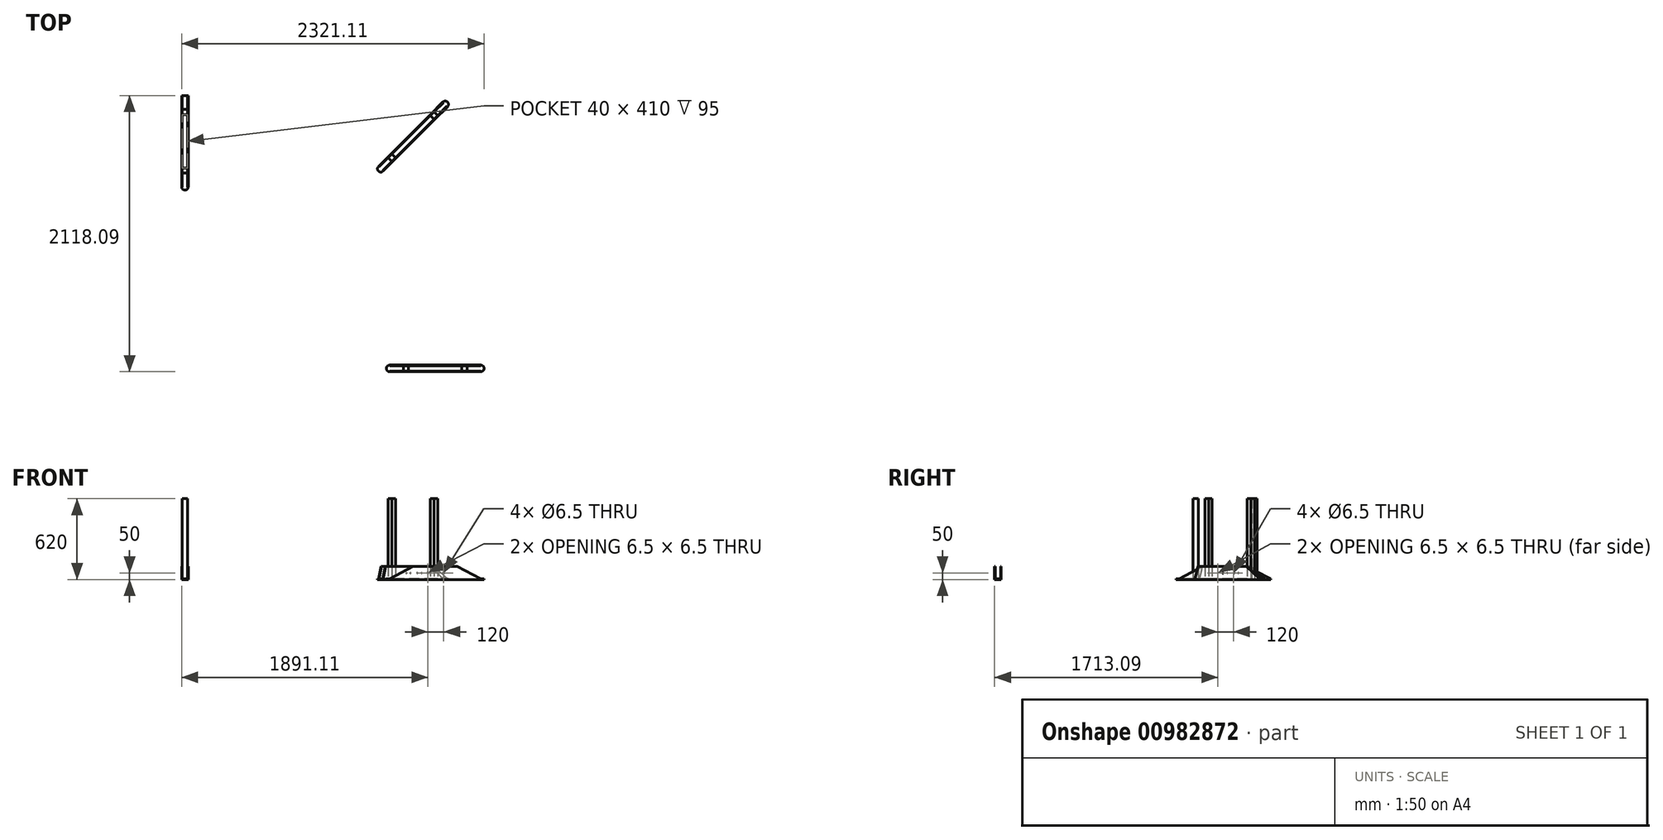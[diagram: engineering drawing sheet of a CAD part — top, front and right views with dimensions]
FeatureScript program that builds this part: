
annotation { "Feature Type Name" : "Feature", "Feature Type Description" : "" }
export const myFeature = defineFeature(function(context is Context, id is Id, definition is map)
    precondition{}
    {
        {
            var Q0;
            Q0=qCreatedBy(makeId("Top.planeOp"),FACE);
            var sketch = newSketch(context, id + "F0", { "sketchPlane" : qUnion([Q0])});
            skLineSegment(sketch, "E0", {"start": v(-1484.96, 152.2) * mm, "end": v(-1484.96, 852.2) * mm});
            skLineSegment(sketch, "E1", {"start": v(-1434.96, 852.2) * mm, "end": v(-1434.96, 152.2) * mm});
            skLineSegment(sketch, "E2.left", {"start": v(-1479.96, 502.2) * mm, "end": v(-1479.96, 542.2) * mm});
            skLineSegment(sketch, "E2.right", {"start": v(-1439.96, 502.2) * mm, "end": v(-1439.96, 542.2) * mm});
            skLineSegment(sketch, "E3.left", {"start": v(-1479.96, 202.2) * mm, "end": v(-1479.96, 242.2) * mm});
            skLineSegment(sketch, "E3.right", {"start": v(-1439.96, 202.2) * mm, "end": v(-1439.96, 242.2) * mm});
            skLineSegment(sketch, "E4", {"start": v(111.15, -1215.89) * mm, "end": v(811.15, -1215.89) * mm});
            skLineSegment(sketch, "E5", {"start": v(811.15, -1265.89) * mm, "end": v(111.15, -1265.89) * mm});
            skLineSegment(sketch, "E6.bottom", {"start": v(331.15, -1260.89) * mm, "end": v(421.15, -1260.89) * mm});
            skLineSegment(sketch, "E6.top", {"start": v(331.15, -1220.89) * mm, "end": v(421.15, -1220.89) * mm});
            skLineSegment(sketch, "E7.bottom", {"start": v(511.15, -1260.89) * mm, "end": v(591.15, -1260.89) * mm});
            skLineSegment(sketch, "E7.top", {"start": v(511.15, -1220.89) * mm, "end": v(591.15, -1220.89) * mm});
            skLineSegment(sketch, "E8", {"start": v(43.16, 326.14) * mm, "end": v(392.98, 675.97) * mm});
            skLineSegment(sketch, "E9", {"start": v(78.51, 290.79) * mm, "end": v(428.33, 640.61) * mm});
            skLineSegment(sketch, "E10", {"start": v(428.33, 640.61) * mm, "end": v(449.74, 662.02) * mm});
            skLineSegment(sketch, "E11", {"start": v(392.98, 675.97) * mm, "end": v(414.39, 697.38) * mm});
            skLineSegment(sketch, "E12", {"start": v(414.39, 697.38) * mm, "end": v(446.01, 729) * mm});
            skLineSegment(sketch, "E13", {"start": v(485.1, 697.38) * mm, "end": v(449.74, 662.02) * mm});
            skLineSegment(sketch, "E14", {"start": v(485.1, 697.38) * mm, "end": v(555.8, 768.09) * mm});
            skLineSegment(sketch, "E15", {"start": v(555.8, 768.09) * mm, "end": v(520.45, 803.44) * mm});
            skLineSegment(sketch, "E16", {"start": v(520.45, 803.44) * mm, "end": v(446.01, 729) * mm});
            skLineSegment(sketch, "E17", {"start": v(78.51, 290.79) * mm, "end": v(60.83, 273.11) * mm});
            skLineSegment(sketch, "E18", {"start": v(43.16, 326.14) * mm, "end": v(25.48, 308.47) * mm});
            skLineSegment(sketch, "E19", {"start": v(241.15, 517.06) * mm, "end": v(269.43, 545.35) * mm});
            skLineSegment(sketch, "E20", {"start": v(297.71, 517.06) * mm, "end": v(269.43, 488.78) * mm});
            skLineSegment(sketch, "E21", {"start": v(280.23, 556.15) * mm, "end": v(308.52, 584.43) * mm});
            skLineSegment(sketch, "E22", {"start": v(333.07, 552.42) * mm, "end": v(304.79, 524.13) * mm});
            skLineSegment(sketch, "E23", {"start": v(-1484.96, 852.2) * mm, "end": v(-1434.96, 852.2) * mm});
            skLineSegment(sketch, "E24", {"start": v(-1484.96, 152.2) * mm, "end": v(-1434.96, 152.2) * mm});
            skLineSegment(sketch, "E25", {"start": v(811.15, -1215.89) * mm, "end": v(811.15, -1265.89) * mm});
            skLineSegment(sketch, "E26", {"start": v(111.15, -1215.89) * mm, "end": v(111.15, -1265.89) * mm});
            skLineSegment(sketch, "E27", {"start": v(25.48, 308.47) * mm, "end": v(60.83, 273.11) * mm});
            skLineSegment(sketch, "E28", {"start": v(241.15, 517.06) * mm, "end": v(29.01, 304.93) * mm});
            skLineSegment(sketch, "E29", {"start": v(269.43, 488.78) * mm, "end": v(57.3, 276.65) * mm});
            skLineSegment(sketch, "E30", {"start": v(297.71, 517.06) * mm, "end": v(552.27, 771.62) * mm});
            skLineSegment(sketch, "E31", {"start": v(269.43, 545.35) * mm, "end": v(523.99, 799.9) * mm});
            skLineSegment(sketch, "E32", {"start": v(511.15, -1260.89) * mm, "end": v(811.15, -1260.89) * mm});
            skLineSegment(sketch, "E33", {"start": v(511.15, -1220.89) * mm, "end": v(811.15, -1220.89) * mm});
            skLineSegment(sketch, "E34", {"start": v(591.15, -1220.89) * mm, "end": v(111.15, -1220.89) * mm});
            skLineSegment(sketch, "E35", {"start": v(591.15, -1260.89) * mm, "end": v(111.15, -1260.89) * mm});
            skLineSegment(sketch, "E36", {"start": v(-1439.96, 202.2) * mm, "end": v(-1439.96, 152.2) * mm});
            skLineSegment(sketch, "E37", {"start": v(-1479.96, 202.2) * mm, "end": v(-1479.96, 152.2) * mm});
            skLineSegment(sketch, "E38", {"start": v(-1479.96, 242.2) * mm, "end": v(-1479.96, 852.2) * mm});
            skLineSegment(sketch, "E39", {"start": v(-1439.96, 242.2) * mm, "end": v(-1439.96, 852.2) * mm});
            skArc(sketch, "E40", {"start": v(-1484.96, 152.2) * mm, "mid": v(-1459.96, 127.2) * mm, "end": v(-1434.96, 152.2) * mm});
            skArc(sketch, "E41", {"start": v(-1484.96, 852.2) * mm, "mid": v(-1459.96, 877.2) * mm, "end": v(-1434.96, 852.2) * mm});
            skArc(sketch, "E42", {"start": v(25.48, 308.47) * mm, "mid": v(25.48, 273.11) * mm, "end": v(60.83, 273.11) * mm});
            skArc(sketch, "E43", {"start": v(555.8, 768.09) * mm, "mid": v(555.8, 803.44) * mm, "end": v(520.45, 803.44) * mm});
            skArc(sketch, "E44", {"start": v(811.15, -1265.89) * mm, "mid": v(836.15, -1240.89) * mm, "end": v(811.15, -1215.89) * mm});
            skArc(sketch, "E45", {"start": v(111.15, -1215.89) * mm, "mid": v(86.15, -1240.89) * mm, "end": v(111.15, -1265.89) * mm});
            skLineSegment(sketch, "E46.bottom", {"start": v(-1479.96, 747.2) * mm, "end": v(-1439.96, 747.2) * mm});
            skLineSegment(sketch, "E46.top", {"start": v(-1479.96, 707.2) * mm, "end": v(-1439.96, 707.2) * mm});
            skLineSegment(sketch, "E46.left", {"start": v(-1479.96, 747.2) * mm, "end": v(-1479.96, 707.2) * mm});
            skLineSegment(sketch, "E46.right", {"start": v(-1439.96, 747.2) * mm, "end": v(-1439.96, 707.2) * mm});
            skLineSegment(sketch, "E47.bottom", {"start": v(-1439.96, 257.2) * mm, "end": v(-1479.96, 257.2) * mm});
            skLineSegment(sketch, "E47.top", {"start": v(-1439.96, 297.2) * mm, "end": v(-1479.96, 297.2) * mm});
            skLineSegment(sketch, "E47.left", {"start": v(-1439.96, 257.2) * mm, "end": v(-1439.96, 297.2) * mm});
            skLineSegment(sketch, "E47.right", {"start": v(-1479.96, 257.2) * mm, "end": v(-1479.96, 297.2) * mm});
            skLineSegment(sketch, "E48.bottom", {"start": v(216.15, -1260.89) * mm, "end": v(256.15, -1260.89) * mm});
            skLineSegment(sketch, "E48.top", {"start": v(216.15, -1220.89) * mm, "end": v(256.15, -1220.89) * mm});
            skLineSegment(sketch, "E48.left", {"start": v(216.15, -1260.89) * mm, "end": v(216.15, -1220.89) * mm});
            skLineSegment(sketch, "E48.right", {"start": v(256.15, -1260.89) * mm, "end": v(256.15, -1220.89) * mm});
            skLineSegment(sketch, "E49.bottom", {"start": v(666.15, -1260.89) * mm, "end": v(706.15, -1260.89) * mm});
            skLineSegment(sketch, "E49.top", {"start": v(666.15, -1220.89) * mm, "end": v(706.15, -1220.89) * mm});
            skLineSegment(sketch, "E49.left", {"start": v(666.15, -1260.89) * mm, "end": v(666.15, -1220.89) * mm});
            skLineSegment(sketch, "E49.right", {"start": v(706.15, -1260.89) * mm, "end": v(706.15, -1220.89) * mm});
            skLineSegment(sketch, "E50", {"start": v(128, 347.36) * mm, "end": v(99.72, 375.64) * mm});
            skLineSegment(sketch, "E51", {"start": v(156.3, 375.64) * mm, "end": v(128, 403.93) * mm});
            skLineSegment(sketch, "E52", {"start": v(481.56, 700.91) * mm, "end": v(453.28, 729.2) * mm});
            skLineSegment(sketch, "E53", {"start": v(453.28, 672.63) * mm, "end": v(425, 700.91) * mm});
            skSolve(sketch);
        }
        {
            var Q0;
            {var subQ0=sQuery(id+"F0.wireOp",EDGE,"E6.left");Q0=makeQuery(id+"F0.imprint","IMPRINT",FACE,{"disambiguationData":[TD([[makeQuery(id+"F0.imprint","IMPRINT",EDGE,{"derivedFrom":subQ0}),1.0]])]});}
            var Q1;
            {var subQ0=sQuery(id+"F0.wireOp",EDGE,"E6.right");Q1=makeQuery(id+"F0.imprint","IMPRINT",FACE,{"disambiguationData":[TD([[makeQuery(id+"F0.imprint","IMPRINT",EDGE,{"derivedFrom":subQ0}),-1.0]])]});}
            var Q2;
            Q2=makeQuery(id+"F0.imprint","IMPRINT",FACE,{"disambiguationData":[TD([[makeQuery(id+"F0.imprint","IMPRINT",EDGE,{"derivedFrom":sQuery(id+"F0.wireOp",EDGE,"E7.right")}),-1.0]])]});
            var Q3;
            {var subQ0=sQuery(id+"F0.wireOp",EDGE,"E44");Q3=makeQuery(id+"F0.imprint","IMPRINT",FACE,{"disambiguationData":[TD([[makeQuery(id+"F0.imprint","IMPRINT",EDGE,{"derivedFrom":subQ0}),1.0]])]});}
            var Q4;
            {var subQ0=sQuery(id+"F0.wireOp",EDGE,"E45");Q4=makeQuery(id+"F0.imprint","IMPRINT",FACE,{"disambiguationData":[TD([[makeQuery(id+"F0.imprint","IMPRINT",EDGE,{"derivedFrom":subQ0}),1.0]])]});}
            var Q5;
            {var subQ0=sQuery(id+"F0.wireOp",EDGE,"E42");Q5=makeQuery(id+"F0.imprint","IMPRINT",FACE,{"disambiguationData":[TD([[makeQuery(id+"F0.imprint","IMPRINT",EDGE,{"derivedFrom":subQ0}),1.0]])]});}
            var Q6;
            Q6=makeQuery(id+"F0.imprint","IMPRINT",FACE,{"disambiguationData":[TD([[makeQuery(id+"F0.imprint","IMPRINT",EDGE,{"derivedFrom":sQuery(id+"F0.wireOp",EDGE,"d1bdfd27-d275-4df7-8525-5a3e29133dde")}),1.0]])]});
            var Q7;
            {var subQ0=sQuery(id+"F0.wireOp",EDGE,"a0a4fd81-97b6-4ab5-b91d-3bcc11f45807");Q7=makeQuery(id+"F0.imprint","IMPRINT",FACE,{"disambiguationData":[TD([[makeQuery(id+"F0.imprint","IMPRINT",EDGE,{"derivedFrom":subQ0}),1.0]])]});}
            var Q8;
            {var subQ5=sQuery(id+"F0.wireOp",EDGE,"5f6abebd-f6dd-4679-b2fa-9a6ba4823ef2");Q8=makeQuery(id+"F0.imprint","IMPRINT",FACE,{"disambiguationData":[TD([[makeQuery(id+"F0.imprint","IMPRINT",EDGE,{"derivedFrom":subQ5}),1.0]])]});}
            var Q9;
            {var subQ0=sQuery(id+"F0.wireOp",EDGE,"E43");Q9=makeQuery(id+"F0.imprint","IMPRINT",FACE,{"disambiguationData":[TD([[makeQuery(id+"F0.imprint","IMPRINT",EDGE,{"derivedFrom":subQ0}),1.0]])]});}
            var Q10;
            {var subQ0=sQuery(id+"F0.wireOp",EDGE,"E40");Q10=makeQuery(id+"F0.imprint","IMPRINT",FACE,{"disambiguationData":[TD([[makeQuery(id+"F0.imprint","IMPRINT",EDGE,{"derivedFrom":subQ0}),1.0]])]});}
            var Q11;
            Q11=makeQuery(id+"F0.imprint","IMPRINT",FACE,{"disambiguationData":[TD([[makeQuery(id+"F0.imprint","IMPRINT",EDGE,{"derivedFrom":sQuery(id+"F0.wireOp",EDGE,"E3.bottom")}),-1.0]])]});
            var Q12;
            {var subQ0=sQuery(id+"F0.wireOp",EDGE,"E2.bottom");Q12=makeQuery(id+"F0.imprint","IMPRINT",FACE,{"disambiguationData":[TD([[makeQuery(id+"F0.imprint","IMPRINT",EDGE,{"derivedFrom":subQ0}),-1.0]])]});}
            var Q13;
            {var subQ0=sQuery(id+"F0.wireOp",EDGE,"E41");Q13=makeQuery(id+"F0.imprint","IMPRINT",FACE,{"disambiguationData":[TD([[makeQuery(id+"F0.imprint","IMPRINT",EDGE,{"derivedFrom":subQ0}),-1.0]])]});}
            var Q14;
            {var subQ0=sQuery(id+"F0.wireOp",EDGE,"E2.top");Q14=makeQuery(id+"F0.imprint","IMPRINT",FACE,{"disambiguationData":[TD([[makeQuery(id+"F0.imprint","IMPRINT",EDGE,{"derivedFrom":subQ0}),1.0]])]});}
            var Q15;
            {var subQ3=sQuery(id+"F0.wireOp",EDGE,"E3.left");Q15=makeQuery(id+"F0.imprint","IMPRINT",FACE,{"disambiguationData":[TD([[makeQuery(id+"F0.imprint","IMPRINT",EDGE,{"derivedFrom":subQ3}),-1.0]])]});}
            var Q16;
            {var subQ5=sQuery(id+"F0.wireOp",EDGE,"xkCS3JtT-tGRa-9SgF-1onI-mmZA8H57qGDA");Q16=makeQuery(id+"F0.imprint","IMPRINT",FACE,{"disambiguationData":[TD([[makeQuery(id+"F0.imprint","IMPRINT",EDGE,{"derivedFrom":subQ5}),1.0]])]});}
            var Q17;
            {var subQ5=sQuery(id+"F0.wireOp",EDGE,"E48.left");Q17=makeQuery(id+"F0.imprint","IMPRINT",FACE,{"disambiguationData":[TD([[makeQuery(id+"F0.imprint","IMPRINT",EDGE,{"derivedFrom":subQ5}),1.0]])]});}
            var Q18;
            {var subQ0=sQuery(id+"F0.wireOp",EDGE,"E48.right");Q18=makeQuery(id+"F0.imprint","IMPRINT",FACE,{"disambiguationData":[TD([[makeQuery(id+"F0.imprint","IMPRINT",EDGE,{"derivedFrom":subQ0}),-1.0]])]});}
            var Q19;
            {var subQ5=sQuery(id+"F0.wireOp",EDGE,"E49.right");Q19=makeQuery(id+"F0.imprint","IMPRINT",FACE,{"disambiguationData":[TD([[makeQuery(id+"F0.imprint","IMPRINT",EDGE,{"derivedFrom":subQ5}),-1.0]])]});}
            var Q20;
            {var subQ5=sQuery(id+"F0.wireOp",EDGE,"E50");Q20=makeQuery(id+"F0.imprint","IMPRINT",FACE,{"disambiguationData":[TD([[makeQuery(id+"F0.imprint","IMPRINT",EDGE,{"derivedFrom":subQ5}),1.0]])]});}
            var Q21;
            {var subQ5=sQuery(id+"F0.wireOp",EDGE,"E52");Q21=makeQuery(id+"F0.imprint","IMPRINT",FACE,{"disambiguationData":[TD([[makeQuery(id+"F0.imprint","IMPRINT",EDGE,{"derivedFrom":subQ5}),-1.0]])]});}
            var Q22;
            {var subQ0=sQuery(id+"F0.wireOp",EDGE,"E46.top");Q22=makeQuery(id+"F0.imprint","IMPRINT",FACE,{"disambiguationData":[TD([[makeQuery(id+"F0.imprint","IMPRINT",EDGE,{"derivedFrom":subQ0}),-1.0]])]});}
            var Q23;
            {var subQ5=sQuery(id+"F0.wireOp",EDGE,"E46.bottom");Q23=makeQuery(id+"F0.imprint","IMPRINT",FACE,{"disambiguationData":[TD([[makeQuery(id+"F0.imprint","IMPRINT",EDGE,{"derivedFrom":subQ5}),1.0]])]});}
            var Q24;
            {var subQ8=sQuery(id+"F0.wireOp",EDGE,"E19");Q24=makeQuery(id+"F0.imprint","IMPRINT",FACE,{"disambiguationData":[TD([[makeQuery(id+"F0.imprint","IMPRINT",EDGE,{"derivedFrom":subQ8}),-1.0]])]});}
            extrude(context, id + "F1", {"entities" : qUnion([Q0, Q1, Q2, Q3, Q4, Q5, Q6, Q7, Q8, Q9, Q10, Q11, Q12, Q13, Q14, Q15, Q16, Q17, Q18, Q19, Q20, Q21, Q22, Q23, Q24]), "depth" : 5 * mm, "offsetDistance" : 25 * mm});
        }
        {
            var Q0;
            {var subQ0=sQuery(id+"F0.wireOp",EDGE,"E50");Q0=makeQuery(id+"F0.imprint","IMPRINT",FACE,{"disambiguationData":[TD([[makeQuery(id+"F0.imprint","IMPRINT",EDGE,{"derivedFrom":subQ0}),-1.0]])]});}
            var Q1;
            {var subQ0=sQuery(id+"F0.wireOp",EDGE,"E52");Q1=makeQuery(id+"F0.imprint","IMPRINT",FACE,{"disambiguationData":[TD([[makeQuery(id+"F0.imprint","IMPRINT",EDGE,{"derivedFrom":subQ0}),1.0]])]});}
            var Q2;
            Q2=makeQuery(id+"F0.imprint","IMPRINT",FACE,{"disambiguationData":[TD([[makeQuery(id+"F0.imprint","IMPRINT",EDGE,{"derivedFrom":sQuery(id+"F0.wireOp",EDGE,"E49.bottom")}),1.0]])]});
            var Q3;
            Q3=makeQuery(id+"F0.imprint","IMPRINT",FACE,{"disambiguationData":[TD([[makeQuery(id+"F0.imprint","IMPRINT",EDGE,{"derivedFrom":sQuery(id+"F0.wireOp",EDGE,"E48.bottom")}),1.0]])]});
            var Q4;
            Q4=makeQuery(id+"F0.imprint","IMPRINT",FACE,{"disambiguationData":[TD([[makeQuery(id+"F0.imprint","IMPRINT",EDGE,{"derivedFrom":sQuery(id+"F0.wireOp",EDGE,"E46.bottom")}),-1.0]])]});
            var Q5;
            Q5=makeQuery(id+"F0.imprint","IMPRINT",FACE,{"disambiguationData":[TD([[makeQuery(id+"F0.imprint","IMPRINT",EDGE,{"derivedFrom":sQuery(id+"F0.wireOp",EDGE,"E47.bottom")}),-1.0]])]});
            extrude(context, id + "F2", {"entities" : qUnion([Q0, Q1, Q2, Q3, Q4, Q5]), "depth" : 620 * mm, "offsetDistance" : 25 * mm});
        }
        {
            var Q0;
            {var subQ1=sQuery(id+"F0.wireOp",EDGE,"E0");Q0=makeQuery(id+"F0.imprint","IMPRINT",FACE,{"disambiguationData":[TD([[makeQuery(id+"F0.imprint","IMPRINT",EDGE,{"derivedFrom":subQ1}),-1.0]])]});}
            var Q1;
            {var subQ1=sQuery(id+"F0.wireOp",EDGE,"E1");Q1=makeQuery(id+"F0.imprint","IMPRINT",FACE,{"disambiguationData":[TD([[makeQuery(id+"F0.imprint","IMPRINT",EDGE,{"derivedFrom":subQ1}),-1.0]])]});}
            var Q2;
            Q2=makeQuery(id+"F0.imprint","IMPRINT",FACE,{"disambiguationData":[TD([[makeQuery(id+"F0.imprint","IMPRINT",EDGE,{"derivedFrom":sQuery(id+"F0.wireOp",EDGE,"E8")}),-1.0]])]});
            var Q3;
            Q3=makeQuery(id+"F0.imprint","IMPRINT",FACE,{"disambiguationData":[TD([[makeQuery(id+"F0.imprint","IMPRINT",EDGE,{"derivedFrom":sQuery(id+"F0.wireOp",EDGE,"E9")}),1.0]])]});
            var Q4;
            {var subQ1=sQuery(id+"F0.wireOp",EDGE,"E4");Q4=makeQuery(id+"F0.imprint","IMPRINT",FACE,{"disambiguationData":[TD([[makeQuery(id+"F0.imprint","IMPRINT",EDGE,{"derivedFrom":subQ1}),-1.0]])]});}
            var Q5;
            {var subQ1=sQuery(id+"F0.wireOp",EDGE,"E5");Q5=makeQuery(id+"F0.imprint","IMPRINT",FACE,{"disambiguationData":[TD([[makeQuery(id+"F0.imprint","IMPRINT",EDGE,{"derivedFrom":subQ1}),-1.0]])]});}
            extrude(context, id + "F3", {"entities" : qUnion([Q0, Q1, Q2, Q3, Q4, Q5]), "depth" : 100 * mm, "offsetDistance" : 25 * mm});
        }
        {
            var Q0;
            {var subQ0=sQuery(id+"F0.wireOp",EDGE,"E26");Q0=makeQuery(id+"F3.opExtrude","CAP_EDGE",EDGE,{"disambiguationData":[OSD([subQ0]),TDD([makeQuery(id+"F0.imprint","IMPRINT",EDGE,{"disambiguationData":[TD([[makeQuery(id+"F0.imprint","INTERSECT",VERTEX,{"derivedFrom":[subQ0,sQuery(id+"F0.wireOp",EDGE,"E35")]}),-1.0]])],"derivedFrom":subQ0})])],"isStart":false});}
            var Q1;
            {var subQ0=sQuery(id+"F0.wireOp",EDGE,"E26");Q1=makeQuery(id+"F3.opExtrude","CAP_EDGE",EDGE,{"disambiguationData":[OSD([subQ0]),TDD([makeQuery(id+"F0.imprint","IMPRINT",EDGE,{"disambiguationData":[TD([[makeQuery(id+"F0.imprint","INTERSECT",VERTEX,{"derivedFrom":[subQ0,sQuery(id+"F0.wireOp",EDGE,"E34")]}),1.0]])],"derivedFrom":subQ0})])],"isStart":false});}
            var Q2;
            {var subQ0=sQuery(id+"F0.wireOp",EDGE,"E25");Q2=makeQuery(id+"F3.opExtrude","CAP_EDGE",EDGE,{"disambiguationData":[OSD([subQ0]),TDD([makeQuery(id+"F0.imprint","IMPRINT",EDGE,{"disambiguationData":[TD([[makeQuery(id+"F0.imprint","INTERSECT",VERTEX,{"derivedFrom":[subQ0,sQuery(id+"F0.wireOp",EDGE,"E32")]}),-1.0]])],"derivedFrom":subQ0})])],"isStart":false});}
            var Q3;
            {var subQ0=sQuery(id+"F0.wireOp",EDGE,"E25");Q3=makeQuery(id+"F3.opExtrude","CAP_EDGE",EDGE,{"disambiguationData":[OSD([subQ0]),TDD([makeQuery(id+"F0.imprint","IMPRINT",EDGE,{"disambiguationData":[TD([[makeQuery(id+"F0.imprint","INTERSECT",VERTEX,{"derivedFrom":[subQ0,sQuery(id+"F0.wireOp",EDGE,"E33")]}),1.0]])],"derivedFrom":subQ0})])],"isStart":false});}
            chamfer(context, id + "F4", {"entities" : qUnion([Q0, Q1, Q2, Q3]), "chamferType" : ChamferType.TWO_OFFSETS, "width1" : 180 * mm, "oppositeDirection" : false, "width2" : 95 * mm, "tangentPropagation" : true});
        }
        {
            var Q0;
            {var subQ0=sQuery(id+"F0.wireOp",EDGE,"E23");Q0=makeQuery(id+"F3.opExtrude","CAP_EDGE",EDGE,{"disambiguationData":[OSD([subQ0]),TDD([makeQuery(id+"F0.imprint","IMPRINT",EDGE,{"disambiguationData":[TD([[makeQuery(id+"F0.imprint","INTERSECT",VERTEX,{"derivedFrom":[subQ0,sQuery(id+"F0.wireOp",EDGE,"E39")]}),-1.0]])],"derivedFrom":subQ0})])],"isStart":false});}
            var Q1;
            {var subQ0=sQuery(id+"F0.wireOp",EDGE,"E23");Q1=makeQuery(id+"F3.opExtrude","CAP_EDGE",EDGE,{"disambiguationData":[OSD([subQ0]),TDD([makeQuery(id+"F0.imprint","IMPRINT",EDGE,{"disambiguationData":[TD([[makeQuery(id+"F0.imprint","INTERSECT",VERTEX,{"derivedFrom":[subQ0,sQuery(id+"F0.wireOp",EDGE,"E38")]}),1.0]])],"derivedFrom":subQ0})])],"isStart":false});}
            var Q2;
            {var subQ0=sQuery(id+"F0.wireOp",EDGE,"E24");Q2=makeQuery(id+"F3.opExtrude","CAP_EDGE",EDGE,{"disambiguationData":[OSD([subQ0]),TDD([makeQuery(id+"F0.imprint","IMPRINT",EDGE,{"disambiguationData":[TD([[makeQuery(id+"F0.imprint","INTERSECT",VERTEX,{"derivedFrom":[subQ0,sQuery(id+"F0.wireOp",EDGE,"E37")]}),1.0]])],"derivedFrom":subQ0})])],"isStart":false});}
            var Q3;
            {var subQ0=sQuery(id+"F0.wireOp",EDGE,"E24");Q3=makeQuery(id+"F3.opExtrude","CAP_EDGE",EDGE,{"disambiguationData":[OSD([subQ0]),TDD([makeQuery(id+"F0.imprint","IMPRINT",EDGE,{"disambiguationData":[TD([[makeQuery(id+"F0.imprint","INTERSECT",VERTEX,{"derivedFrom":[subQ0,sQuery(id+"F0.wireOp",EDGE,"E36")]}),-1.0]])],"derivedFrom":subQ0})])],"isStart":false});}
            chamfer(context, id + "F5", {"entities" : qUnion([Q0, Q1, Q2, Q3]), "chamferType" : ChamferType.TWO_OFFSETS, "width1" : 95 * mm, "oppositeDirection" : false, "width2" : 180 * mm, "tangentPropagation" : true});
        }
        {
            var Q0;
            {var subQ0=sQuery(id+"F0.wireOp",EDGE,"E15");Q0=makeQuery(id+"F3.opExtrude","CAP_EDGE",EDGE,{"disambiguationData":[OSD([subQ0]),TDD([makeQuery(id+"F0.imprint","IMPRINT",EDGE,{"disambiguationData":[TD([[makeQuery(id+"F0.imprint","INTERSECT",VERTEX,{"derivedFrom":[subQ0,sQuery(id+"F0.wireOp",EDGE,"E30")]}),1.0]])],"derivedFrom":subQ0})])],"isStart":false});}
            var Q1;
            {var subQ0=sQuery(id+"F0.wireOp",EDGE,"E15");Q1=makeQuery(id+"F3.opExtrude","CAP_EDGE",EDGE,{"disambiguationData":[OSD([subQ0]),TDD([makeQuery(id+"F0.imprint","IMPRINT",EDGE,{"disambiguationData":[TD([[makeQuery(id+"F0.imprint","INTERSECT",VERTEX,{"derivedFrom":[subQ0,sQuery(id+"F0.wireOp",EDGE,"E31")]}),-1.0]])],"derivedFrom":subQ0})])],"isStart":false});}
            chamfer(context, id + "F6", {"entities" : qUnion([Q0, Q1]), "chamferType" : ChamferType.TWO_OFFSETS, "width1" : 142 * mm, "oppositeDirection" : false, "width2" : 95 * mm, "tangentPropagation" : true});
        }
        {
            var Q0;
            {var subQ0=sQuery(id+"F0.wireOp",EDGE,"E27");Q0=makeQuery(id+"F3.opExtrude","CAP_EDGE",EDGE,{"disambiguationData":[OSD([subQ0]),TDD([makeQuery(id+"F0.imprint","IMPRINT",EDGE,{"disambiguationData":[TD([[makeQuery(id+"F0.imprint","INTERSECT",VERTEX,{"derivedFrom":[subQ0,sQuery(id+"F0.wireOp",EDGE,"E29")]}),-1.0]])],"derivedFrom":subQ0})])],"isStart":false});}
            var Q1;
            {var subQ0=sQuery(id+"F0.wireOp",EDGE,"E27");Q1=makeQuery(id+"F3.opExtrude","CAP_EDGE",EDGE,{"disambiguationData":[OSD([subQ0]),TDD([makeQuery(id+"F0.imprint","IMPRINT",EDGE,{"disambiguationData":[TD([[makeQuery(id+"F0.imprint","INTERSECT",VERTEX,{"derivedFrom":[subQ0,sQuery(id+"F0.wireOp",EDGE,"E28")]}),1.0]])],"derivedFrom":subQ0})])],"isStart":false});}
            chamfer(context, id + "F7", {"entities" : qUnion([Q0, Q1]), "chamferType" : ChamferType.TWO_OFFSETS, "width1" : 30 * mm, "oppositeDirection" : false, "width2" : 95 * mm, "tangentPropagation" : true});
        }
        {
            var Q0;
            Q0=makeQuery(id+"F3.opExtrude","SWEPT_BODY",BODY,{"disambiguationData":[OSD([sQuery(id+"F0.wireOp",EDGE,"E1"),sQuery(id+"F0.wireOp",EDGE,"E3.right"),sQuery(id+"F0.wireOp",EDGE,"E23"),sQuery(id+"F0.wireOp",EDGE,"E24"),sQuery(id+"F0.wireOp",EDGE,"E36"),sQuery(id+"F0.wireOp",EDGE,"E39"),sQuery(id+"F0.wireOp",EDGE,"E46.right"),sQuery(id+"F0.wireOp",EDGE,"E47.left")])]});
            var Q1;
            Q1=makeQuery(id+"F3.opExtrude","SWEPT_BODY",BODY,{"disambiguationData":[OSD([sQuery(id+"F0.wireOp",EDGE,"E0"),sQuery(id+"F0.wireOp",EDGE,"E3.left"),sQuery(id+"F0.wireOp",EDGE,"E23"),sQuery(id+"F0.wireOp",EDGE,"E24"),sQuery(id+"F0.wireOp",EDGE,"E37"),sQuery(id+"F0.wireOp",EDGE,"E38"),sQuery(id+"F0.wireOp",EDGE,"E46.left"),sQuery(id+"F0.wireOp",EDGE,"E47.right")])]});
            var Q2;
            Q2=makeQuery(id+"F2.opExtrude","SWEPT_BODY",BODY,{"disambiguationData":[OSD([sQuery(id+"F0.wireOp",EDGE,"E46.bottom"),sQuery(id+"F0.wireOp",EDGE,"E46.top"),sQuery(id+"F0.wireOp",EDGE,"E46.left"),sQuery(id+"F0.wireOp",EDGE,"E46.right")])]});
            var Q3;
            Q3=makeQuery(id+"F1.opExtrude","SWEPT_BODY",BODY,{"disambiguationData":[OSD([sQuery(id+"F0.wireOp",EDGE,"E3.left"),sQuery(id+"F0.wireOp",EDGE,"E3.right"),sQuery(id+"F0.wireOp",EDGE,"E24"),sQuery(id+"F0.wireOp",EDGE,"E36"),sQuery(id+"F0.wireOp",EDGE,"E37"),sQuery(id+"F0.wireOp",EDGE,"E38"),sQuery(id+"F0.wireOp",EDGE,"E39"),sQuery(id+"F0.wireOp",EDGE,"E40"),sQuery(id+"F0.wireOp",EDGE,"E47.bottom")])]});
            var Q4;
            Q4=makeQuery(id+"F1.opExtrude","SWEPT_BODY",BODY,{"disambiguationData":[OSD([sQuery(id+"F0.wireOp",EDGE,"E23"),sQuery(id+"F0.wireOp",EDGE,"E38"),sQuery(id+"F0.wireOp",EDGE,"E39"),sQuery(id+"F0.wireOp",EDGE,"E41"),sQuery(id+"F0.wireOp",EDGE,"E46.bottom")])]});
            var Q5;
            Q5=makeQuery(id+"F1.opExtrude","SWEPT_BODY",BODY,{"disambiguationData":[OSD([sQuery(id+"F0.wireOp",EDGE,"E38"),sQuery(id+"F0.wireOp",EDGE,"E39"),sQuery(id+"F0.wireOp",EDGE,"E46.top"),sQuery(id+"F0.wireOp",EDGE,"E47.top")])]});
            var Q6;
            Q6=makeQuery(id+"F2.opExtrude","SWEPT_BODY",BODY,{"disambiguationData":[OSD([sQuery(id+"F0.wireOp",EDGE,"E47.bottom"),sQuery(id+"F0.wireOp",EDGE,"E47.top"),sQuery(id+"F0.wireOp",EDGE,"E47.left"),sQuery(id+"F0.wireOp",EDGE,"E47.right")])]});
            booleanBodies(context, id + "F8", {"operationType" : BooleanOperationType.UNION, "tools" : qUnion([Q0, Q1, Q2, Q3, Q4, Q5, Q6])});
        }
        {
            var Q0;
            Q0=makeQuery(id+"F1.opExtrude","SWEPT_BODY",BODY,{"disambiguationData":[OSD([sQuery(id+"F0.wireOp",EDGE,"E25"),sQuery(id+"F0.wireOp",EDGE,"E32"),sQuery(id+"F0.wireOp",EDGE,"E33"),sQuery(id+"F0.wireOp",EDGE,"E44"),sQuery(id+"F0.wireOp",EDGE,"E49.right")])]});
            var Q1;
            Q1=makeQuery(id+"F1.opExtrude","SWEPT_BODY",BODY,{"disambiguationData":[OSD([sQuery(id+"F0.wireOp",EDGE,"E26"),sQuery(id+"F0.wireOp",EDGE,"E34"),sQuery(id+"F0.wireOp",EDGE,"E35"),sQuery(id+"F0.wireOp",EDGE,"E45"),sQuery(id+"F0.wireOp",EDGE,"E48.left")])]});
            var Q2;
            Q2=makeQuery(id+"F1.opExtrude","SWEPT_BODY",BODY,{"disambiguationData":[OSD([sQuery(id+"F0.wireOp",EDGE,"E32"),sQuery(id+"F0.wireOp",EDGE,"E33"),sQuery(id+"F0.wireOp",EDGE,"E34"),sQuery(id+"F0.wireOp",EDGE,"E35"),sQuery(id+"F0.wireOp",EDGE,"E48.right"),sQuery(id+"F0.wireOp",EDGE,"E49.left")])]});
            var Q3;
            Q3=makeQuery(id+"F2.opExtrude","SWEPT_BODY",BODY,{"disambiguationData":[OSD([sQuery(id+"F0.wireOp",EDGE,"E48.bottom"),sQuery(id+"F0.wireOp",EDGE,"E48.top"),sQuery(id+"F0.wireOp",EDGE,"E48.left"),sQuery(id+"F0.wireOp",EDGE,"E48.right")])]});
            var Q4;
            Q4=makeQuery(id+"F2.opExtrude","SWEPT_BODY",BODY,{"disambiguationData":[OSD([sQuery(id+"F0.wireOp",EDGE,"E49.bottom"),sQuery(id+"F0.wireOp",EDGE,"E49.top"),sQuery(id+"F0.wireOp",EDGE,"E49.left"),sQuery(id+"F0.wireOp",EDGE,"E49.right")])]});
            var Q5;
            Q5=makeQuery(id+"F3.opExtrude","SWEPT_BODY",BODY,{"disambiguationData":[OSD([sQuery(id+"F0.wireOp",EDGE,"E4"),sQuery(id+"F0.wireOp",EDGE,"E25"),sQuery(id+"F0.wireOp",EDGE,"E26"),sQuery(id+"F0.wireOp",EDGE,"E33"),sQuery(id+"F0.wireOp",EDGE,"E34"),sQuery(id+"F0.wireOp",EDGE,"E48.top"),sQuery(id+"F0.wireOp",EDGE,"E49.top")])]});
            var Q6;
            Q6=makeQuery(id+"F3.opExtrude","SWEPT_BODY",BODY,{"disambiguationData":[OSD([sQuery(id+"F0.wireOp",EDGE,"E5"),sQuery(id+"F0.wireOp",EDGE,"E25"),sQuery(id+"F0.wireOp",EDGE,"E26"),sQuery(id+"F0.wireOp",EDGE,"E32"),sQuery(id+"F0.wireOp",EDGE,"E35"),sQuery(id+"F0.wireOp",EDGE,"E48.bottom"),sQuery(id+"F0.wireOp",EDGE,"E49.bottom")])]});
            booleanBodies(context, id + "F9", {"operationType" : BooleanOperationType.UNION, "tools" : qUnion([Q0, Q1, Q2, Q3, Q4, Q5, Q6])});
        }
        {
            var Q0;
            Q0=makeQuery(id+"F3.opExtrude","SWEPT_FACE",FACE,{"disambiguationData":[OSD([sQuery(id+"F0.wireOp",EDGE,"E5")])]});
            var sketch = newSketch(context, id + "F10", { "sketchPlane" : qUnion([Q0])});
            skCircle(sketch, "E54", {"center": v(406.15, 50) * mm, "radius": 3.25 * mm});
            skCircle(sketch, "E55", {"center": v(526.15, 50) * mm, "radius": 3.25 * mm});
            skSolve(sketch);
        }
        {
            var Q0;
            Q0=makeQuery(id+"F10.imprint","IMPRINT",FACE,{"disambiguationData":[TD([[makeQuery(id+"F10.imprint","IMPRINT",EDGE,{"derivedFrom":sQuery(id+"F10.wireOp",EDGE,"E54")}),1.0]])]});
            var Q1;
            Q1=makeQuery(id+"F10.imprint","IMPRINT",FACE,{"disambiguationData":[TD([[makeQuery(id+"F10.imprint","IMPRINT",EDGE,{"derivedFrom":sQuery(id+"F10.wireOp",EDGE,"E55")}),1.0]])]});
            extrude(context, id + "F11", {"entities" : qUnion([Q0, Q1]), "operationType" : NewBodyOperationType.REMOVE, "oppositeDirection" : true, "depth" : 60 * mm, "offsetDistance" : 25 * mm});
        }
        {
            var Q0;
            Q0=makeQuery(id+"F3.opExtrude","SWEPT_FACE",FACE,{"disambiguationData":[OSD([sQuery(id+"F0.wireOp",EDGE,"E9"),sQuery(id+"F0.wireOp",EDGE,"E10"),sQuery(id+"F0.wireOp",EDGE,"E13"),sQuery(id+"F0.wireOp",EDGE,"E14"),sQuery(id+"F0.wireOp",EDGE,"E17")])]});
            var sketch = newSketch(context, id + "F12", { "sketchPlane" : qUnion([Q0])});
            skCircle(sketch, "E56", {"center": v(536.14, 50) * mm, "radius": 3.25 * mm});
            skCircle(sketch, "E57", {"center": v(656.14, 50) * mm, "radius": 3.25 * mm});
            skSolve(sketch);
        }
        {
            var Q0;
            Q0=makeQuery(id+"F12.imprint","IMPRINT",FACE,{"disambiguationData":[TD([[makeQuery(id+"F12.imprint","IMPRINT",EDGE,{"derivedFrom":sQuery(id+"F12.wireOp",EDGE,"E56")}),1.0]])]});
            var Q1;
            Q1=makeQuery(id+"F12.imprint","IMPRINT",FACE,{"disambiguationData":[TD([[makeQuery(id+"F12.imprint","IMPRINT",EDGE,{"derivedFrom":sQuery(id+"F12.wireOp",EDGE,"E57")}),1.0]])]});
            extrude(context, id + "F13", {"entities" : qUnion([Q0, Q1]), "operationType" : NewBodyOperationType.REMOVE, "oppositeDirection" : true, "depth" : 60 * mm, "offsetDistance" : 25 * mm});
        }
        {
            var Q0;
            Q0=makeQuery(id+"F3.opExtrude","SWEPT_FACE",FACE,{"disambiguationData":[OSD([sQuery(id+"F0.wireOp",EDGE,"E0")])]});
            var sketch = newSketch(context, id + "F14", { "sketchPlane" : qUnion([Q0])});
            skCircle(sketch, "E58", {"center": v(-567.2, 50) * mm, "radius": 3.25 * mm});
            skCircle(sketch, "E59", {"center": v(-447.2, 50) * mm, "radius": 3.25 * mm});
            skSolve(sketch);
        }
        {
            var Q0;
            Q0=makeQuery(id+"F14.imprint","IMPRINT",FACE,{"disambiguationData":[TD([[makeQuery(id+"F14.imprint","IMPRINT",EDGE,{"derivedFrom":sQuery(id+"F14.wireOp",EDGE,"E58")}),1.0]])]});
            var Q1;
            Q1=makeQuery(id+"F14.imprint","IMPRINT",FACE,{"disambiguationData":[TD([[makeQuery(id+"F14.imprint","IMPRINT",EDGE,{"derivedFrom":sQuery(id+"F14.wireOp",EDGE,"E59")}),1.0]])]});
            extrude(context, id + "F15", {"entities" : qUnion([Q0, Q1]), "operationType" : NewBodyOperationType.REMOVE, "oppositeDirection" : true, "depth" : 60 * mm, "offsetDistance" : 25 * mm});
        }
    });
